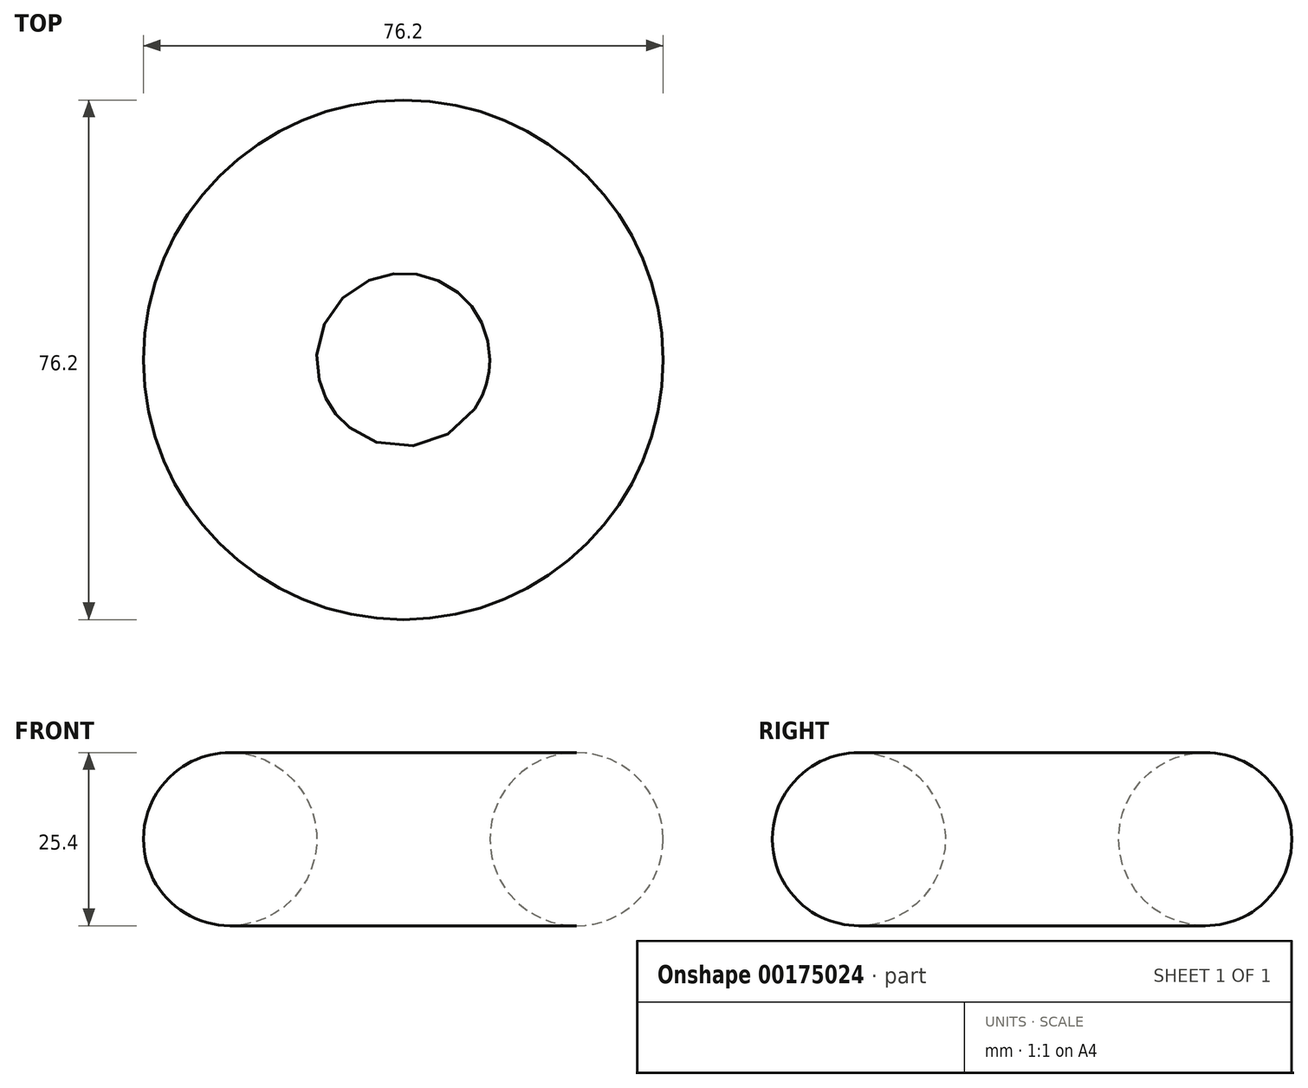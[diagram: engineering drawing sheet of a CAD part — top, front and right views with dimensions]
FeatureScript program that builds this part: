
annotation { "Feature Type Name" : "Feature", "Feature Type Description" : "" }
export const myFeature = defineFeature(function(context is Context, id is Id, definition is map)
    precondition{}
    {
        {
            var Q0;
            Q0=qCreatedBy(makeId("Front.planeOp"),FACE);
            var sketch = newSketch(context, id + "F0", { "sketchPlane" : qUnion([Q0])});
            skCircle(sketch, "E0", {"center": v(0, 0) * mm, "radius": 12.7 * mm});
            skLineSegment(sketch, "E1", {"start": v(25.4, 75.75) * mm, "end": v(25.4, -76.1) * mm});
            skSolve(sketch);
        }
        {
            var Q0;
            Q0=makeQuery(id+"F0.imprint","IMPRINT",FACE,{"disambiguationData":[TD([[makeQuery(id+"F0.imprint","IMPRINT",EDGE,{"derivedFrom":sQuery(id+"F0.wireOp",EDGE,"E0")}),1.0]])]});
            var Q1;
            Q1=sQuery(id+"F0.wireOp",EDGE,"E1");
            revolve(context, id + "F1", {"entities" : qUnion([Q0]), "axis" : qUnion([Q1]), "revolveType" : RevolveType.FULL});
        }
    });
